# Revit family: TYCO-FPP-Zettler-DDM800 Universal fire and gas module
name_source: partatom
category: Electrical Fixtures
revit_build: Autodesk Revit 2014 (Build: 20130308_1515(x64)
units: mm (PartAtom-declared; Revit-internal decimal feet)

## types (1)
- TYCO-FPP-Zettler-DDM800 Universal fire and gas module
    Description = The DDM800 provides the ability to connect and
interface 2 zones of conventional 2 wire fire detectors or
two 4-20mA sensors to the MZX Fire alarm controllers.
    Detector Circuit Current Limit = 25 mA
    Detector Circuit Supply Voltage = 22V nominal, 22.5V max
    EOLs = Conventional Circuit: 4,7 kOhms
    Front cover = Yes
    Keynote = The DDM800 is compatible with MZX Consys version 15
or later.
    Length = 61 mm
    Loop Voltage Max = 40 V DC
    Loop Voltage Min = 28 V DC
    Manufacturer = Tyco
    Model = Zettler - 577.800.006
    Operating Humidity = Up to 95 % RH
    Operating Temperature = -25 to +70 oC
    PCB = PCB
    RT = RT
    Rear cover = Yes
    S = SS1
    Sense Resistor = Value 220 O hms
    Storage Temperature = -40 to +80 oC
    Type Comments = An integral line
isolator is incorporated in the module.
    URL = https://tycosafetyproducts-anz.com
    Width = 84 mm

## geometry (parser evidence)
native form markers: Sweep x8
no freeform markers — native parametric forms only
